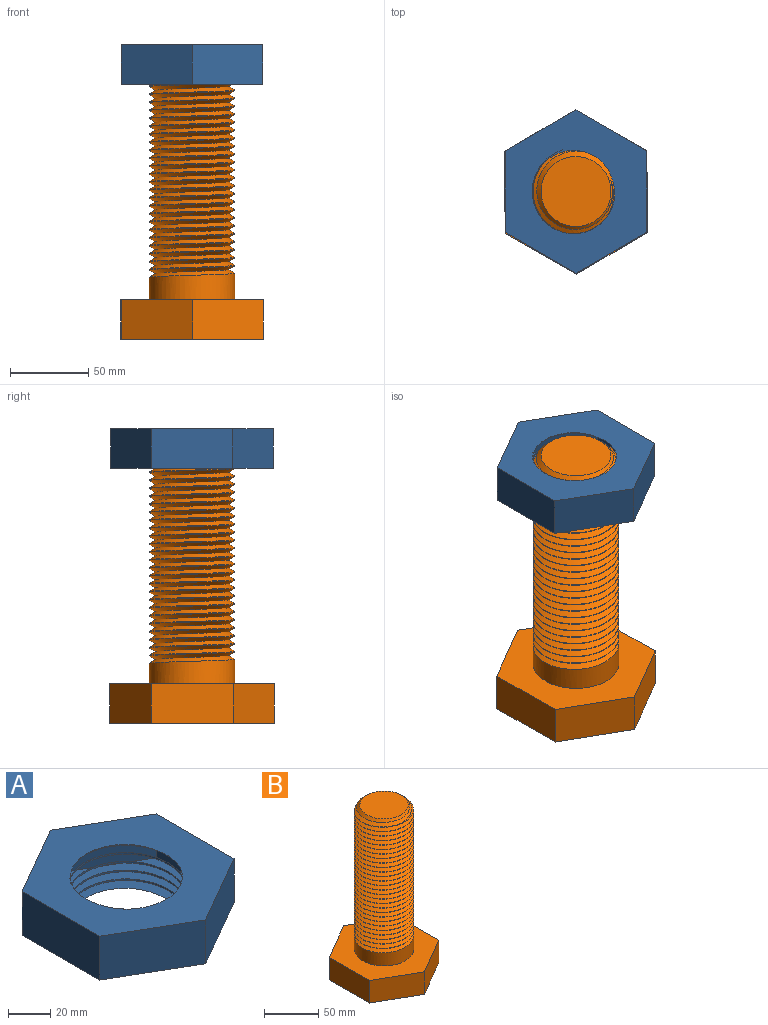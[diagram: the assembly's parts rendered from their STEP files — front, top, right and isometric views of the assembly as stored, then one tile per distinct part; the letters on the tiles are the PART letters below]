
ASSEMBLY  parts=2 mates=1
PART A: 9 faces, bbox 90x103.9x25.4 mm
  f0: plane 103.94x90.01mm, normal (0,0,1), area 4818.1mm2, adj f2,f3,f4,f5,f6,f7,f8
  f1: plane 103.94x90.01mm, normal (0,0,-1), area 4818.1mm2, adj f2,f3,f4,f5,f6,f7,f8
  f2: plane 51.97x25.4mm, normal (1,0,0), area 1320mm2, adj f0,f1,f3,f7
  f3: plane 45.01x25.98mm, normal (0.5,0.87,0), area 1320mm2, adj f0,f1,f2,f4
  f4: plane 45.01x25.98mm, normal (-0.5,0.87,0), area 1320mm2, adj f0,f1,f3,f5
  f5: plane 51.97x25.4mm, normal (-1,0,0), area 1320mm2, adj f0,f1,f4,f6
  f6: plane 45.01x25.98mm, normal (-0.5,-0.87,0), area 1320mm2, adj f0,f1,f5,f7
  f7: plane 45.01x25.98mm, normal (0.5,-0.87,0), area 1320mm2, adj f0,f1,f2,f6
  f8: cylinder r=27.9mm len=55.81mm, axis (0,0,-1), area 822.4mm2, adj f0,f1
PART B: 55 faces, bbox 91.1x104.8x190 mm
  f0: plane 104.78x91.14mm, normal (0,0,-1), area 6282.3mm2, adj f30,f31,f32,f33,f34,f35,f42,f43
  f1: cylinder r=27.4mm len=54.79mm, axis (0,0,-1), area 2444.9mm2, adj f2,f36,f39,f40
  f2: cylinder r=27.4mm len=54.79mm, axis (0,0,-1), area 57.2mm2, adj f1,f3,f40,f41
  f3: cylinder r=27.4mm len=54.79mm, axis (0,0,-1), area 56.5mm2, adj f2,f4,f40,f41
  f4: cylinder r=27.4mm len=54.79mm, axis (0,0,-1), area 57.2mm2, adj f3,f5,f40,f41
  f5: cylinder r=27.4mm len=54.79mm, axis (0,0,-1), area 57.1mm2, adj f4,f6,f40,f41
  f6: cylinder r=27.4mm len=54.79mm, axis (0,0,-1), area 57.1mm2, adj f5,f7,f40,f41
  f7: cylinder r=27.4mm len=54.79mm, axis (0,0,-1), area 57mm2, adj f6,f8,f40,f41
  f8: cylinder r=27.4mm len=54.79mm, axis (0,0,-1), area 56.5mm2, adj f7,f9,f40,f41
  f9: cylinder r=27.4mm len=54.79mm, axis (0,0,-1), area 57.3mm2, adj f8,f10,f40,f41
  f10: cylinder r=27.4mm len=54.79mm, axis (0,0,-1), area 57.2mm2, adj f9,f11,f40,f41
  f11: cylinder r=27.4mm len=54.79mm, axis (0,0,-1), area 56.9mm2, adj f10,f12,f40,f41
  f12: cylinder r=27.4mm len=54.79mm, axis (0,0,-1), area 57mm2, adj f11,f13,f40,f41
  f13: cylinder r=27.4mm len=54.79mm, axis (0,0,-1), area 56.7mm2, adj f12,f14,f40,f41
  f14: cylinder r=27.4mm len=54.79mm, axis (0,0,-1), area 57.4mm2, adj f13,f15,f40,f41
  f15: cylinder r=27.4mm len=54.79mm, axis (0,0,-1), area 57.2mm2, adj f14,f16,f40,f41
  f16: cylinder r=27.4mm len=54.79mm, axis (0,0,-1), area 56.6mm2, adj f15,f17,f40,f41
  f17: cylinder r=27.4mm len=54.79mm, axis (0,0,-1), area 57mm2, adj f16,f18,f40,f41
  f18: cylinder r=27.4mm len=54.79mm, axis (0,0,-1), area 56.9mm2, adj f17,f19,f40,f41
  f19: cylinder r=27.4mm len=54.79mm, axis (0,0,-1), area 57.4mm2, adj f18,f20,f40,f41
  f20: cylinder r=27.4mm len=54.79mm, axis (0,0,-1), area 57.1mm2, adj f19,f21,f40,f41
  f21: cylinder r=27.4mm len=54.79mm, axis (0,0,-1), area 56.5mm2, adj f20,f22,f40,f41
  f22: cylinder r=27.4mm len=54.79mm, axis (0,0,-1), area 57.2mm2, adj f21,f23,f40,f41
  f23: cylinder r=27.4mm len=54.79mm, axis (0,0,-1), area 57mm2, adj f22,f24,f40,f41
  f24: cylinder r=27.4mm len=54.79mm, axis (0,0,-1), area 57.3mm2, adj f23,f25,f40,f41
  f25: cylinder r=27.4mm len=54.79mm, axis (0,0,-1), area 56.9mm2, adj f24,f26,f40,f41
  f26: cylinder r=27.4mm len=54.79mm, axis (0,0,-1), area 56.6mm2, adj f25,f27,f40,f41
  f27: cylinder r=27.4mm len=54.79mm, axis (0,0,-1), area 57.4mm2, adj f26,f28,f40,f41
  f28: cylinder r=27.4mm len=54.79mm, axis (0,0,-1), area 57.1mm2, adj f27,f29,f40,f41
  f29: cylinder r=27.4mm len=54.79mm, axis (0,0,-1), area 42mm2, adj f28,f38,f40,f41
  f30: plane 45.57x25.85mm, normal (0.49,0.87,0), area 1330.8mm2, adj f0,f31,f35,f36
  f31: plane 45.17x26.54mm, normal (-0.51,0.86,0), area 1330.8mm2, adj f0,f30,f32,f36
  f32: plane 52.39x25.4mm, normal (-1,-0.01,0), area 1330.8mm2, adj f0,f31,f33,f36
  f33: plane 45.57x25.85mm, normal (-0.49,-0.87,0), area 1330.8mm2, adj f0,f32,f34,f36
  f34: plane 45.17x26.54mm, normal (0.51,-0.86,0), area 1330.8mm2, adj f0,f33,f35,f36
  f35: plane 52.39x25.4mm, normal (1,0.01,0), area 1330.8mm2, adj f0,f30,f34,f36
  f36: plane 104.78x91.14mm, normal (0,0,1), area 4774mm2, adj f1,f30,f31,f32,f33,f34,f35
  f37: plane 44.63x44.63mm, normal (0,0,1), area 1564.5mm2, adj f38
  f38: cone r=22.32mm half-angle=45deg, axis (0,0,-1), area 676.4mm2, adj f29,f37,f40,f41
  f39: plane 4.75x4.11mm, normal (0,1,0), area 9.8mm2, adj f1,f40,f41
  f40: bspline ~150.54x63.27mm, area 21837.6mm2, adj f1,f2,f3,f4,f5,f6,f7,f8
  f41: bspline ~150.54x63.27mm, area 21591.3mm2, adj f2,f3,f4,f5,f6,f7,f8,f9
  f42: plane 29.37x12.7mm, normal (-1,0,0), area 373mm2, adj f0,f43,f53,f54
  f43: plane 29.37x12.7mm, normal (0,-1,0), area 373mm2, adj f0,f42,f44,f54
  f44: cylinder r=3.17mm len=12.7mm, axis (0,0,-1), area 126.7mm2, adj f0,f43,f45,f54
  f45: plane 29.37x12.7mm, normal (0,1,0), area 373mm2, adj f0,f44,f46,f54
  f46: plane 29.37x12.7mm, normal (-1,0,0), area 373mm2, adj f0,f45,f47,f54
  f47: cylinder r=3.17mm len=12.7mm, axis (0,0,-1), area 126.7mm2, adj f0,f46,f48,f54
  f48: plane 29.37x12.7mm, normal (1,0,0), area 373mm2, adj f0,f47,f49,f54
  f49: plane 29.37x12.7mm, normal (0,1,0), area 373mm2, adj f0,f48,f50,f54
  f50: cylinder r=3.17mm len=12.7mm, axis (0,0,-1), area 126.7mm2, adj f0,f49,f51,f54
  f51: plane 29.37x12.7mm, normal (0,-1,0), area 373mm2, adj f0,f50,f52,f54
  f52: plane 29.37x12.7mm, normal (1,0,0), area 373mm2, adj f0,f51,f53,f54
  f53: cylinder r=3.17mm len=12.7mm, axis (0,0,-1), area 126.7mm2, adj f0,f42,f52,f54
  f54: plane 71.44x71.44mm, normal (0,0,-1), area 849.6mm2, adj f42,f43,f44,f45,f46,f47,f48,f49
PLACE A t=(-197.18,-67.46,-25.56)mm
PLACE B t=(-197.18,-67.46,-143.41)mm
MATE cylindrical B.f1 <-> A.f8  axis (0,0,1) through (-197.18,-67.46,44.55)mm
